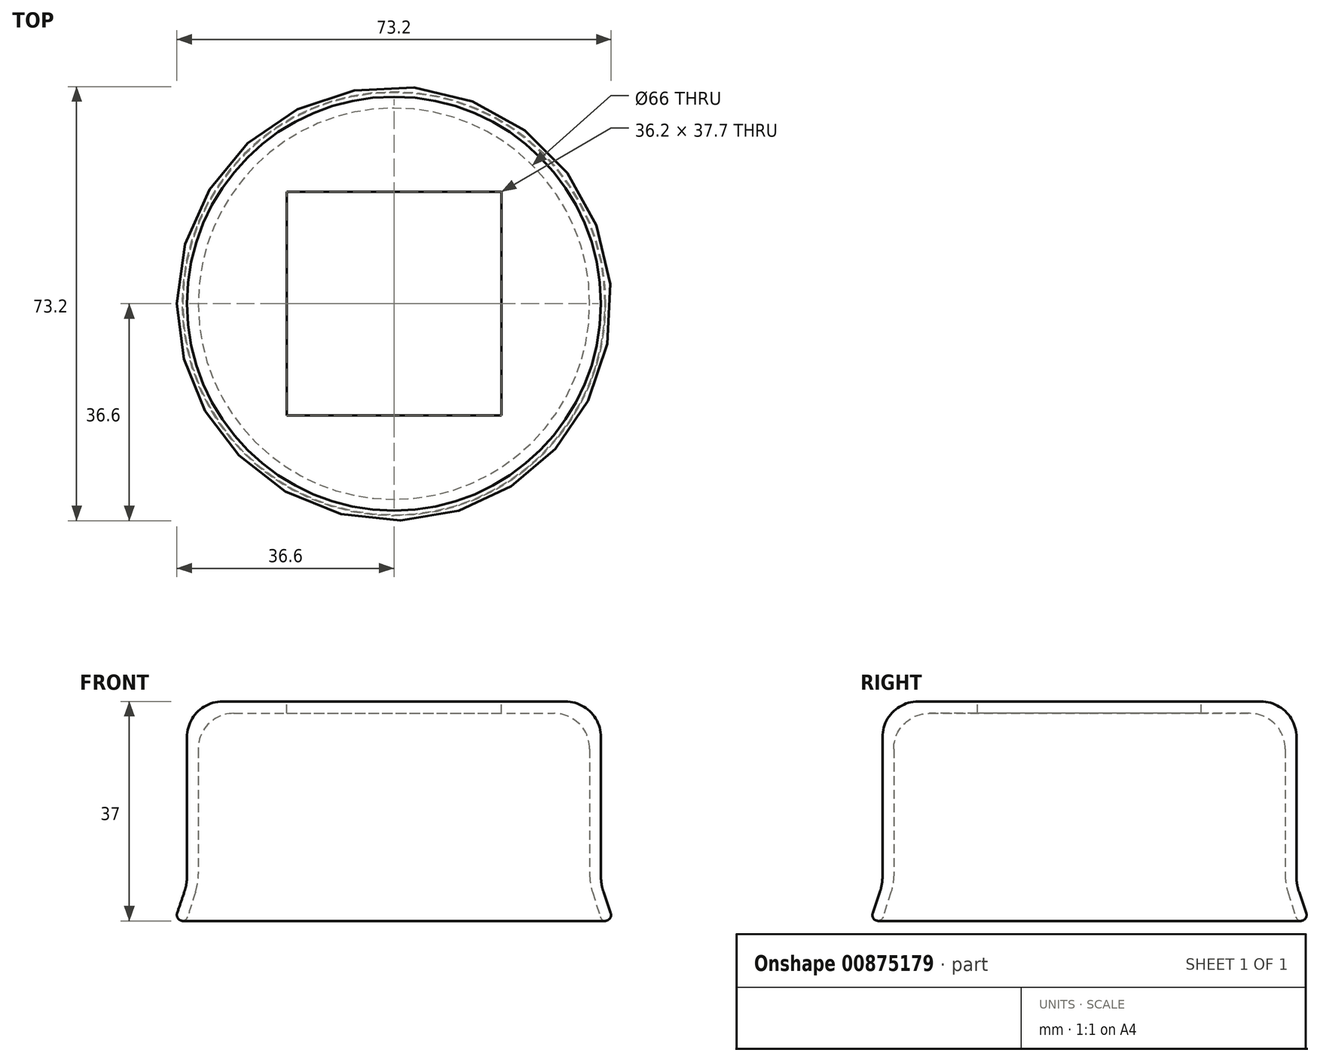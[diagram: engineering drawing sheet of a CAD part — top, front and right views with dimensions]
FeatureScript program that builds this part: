
annotation { "Feature Type Name" : "Feature", "Feature Type Description" : "" }
export const myFeature = defineFeature(function(context is Context, id is Id, definition is map)
    precondition{}
    {
        {
            var Q0;
            Q0=qCreatedBy(makeId("Front.planeOp"),FACE);
            var sketch = newSketch(context, id + "F0", { "sketchPlane" : qUnion([Q0])});
            skLineSegment(sketch, "E0", {"start": v(0, 35) * mm, "end": v(-27, 35) * mm});
            skLineSegment(sketch, "E1", {"start": v(-34.9, 7.5) * mm, "end": v(-34.9, 31) * mm});
            skLineSegment(sketch, "E2", {"start": v(-28.9, 37) * mm, "end": v(0, 37) * mm});
            skLineSegment(sketch, "E3", {"start": v(0, 37) * mm, "end": v(0, 35) * mm});
            skLineSegment(sketch, "E4", {"start": v(-33, 29) * mm, "end": v(-33, 7.9) * mm});
            skPoint(sketch, "E5.visualSharp", {"position": v(-34.9, 37) * mm});
            skArc(sketch, "E5.filletArc", {"start": v(-28.9, 37) * mm, "mid": v(-33.14, 35.24) * mm, "end": v(-34.9, 31) * mm});
            skPoint(sketch, "E6.visualSharp", {"position": v(-33, 35) * mm});
            skArc(sketch, "E6.filletArc", {"start": v(-27, 35) * mm, "mid": v(-31.24, 33.24) * mm, "end": v(-33, 29) * mm});
            skLineSegment(sketch, "E7", {"start": v(-33.46, 4.89) * mm, "end": v(-34.78, 0.7) * mm});
            skLineSegment(sketch, "E8", {"start": v(-35.6, 0) * mm, "end": v(-35.73, 0) * mm});
            skLineSegment(sketch, "E9", {"start": v(-36.55, 1.32) * mm, "end": v(-35.33, 4.91) * mm});
            skPoint(sketch, "E10.visualSharp", {"position": v(-33, 6.35) * mm});
            skArc(sketch, "E10.filletArc", {"start": v(-33.46, 4.89) * mm, "mid": v(-33.12, 6.37) * mm, "end": v(-33, 7.9) * mm});
            skPoint(sketch, "E11.visualSharp", {"position": v(-34.9, 6.17) * mm});
            skArc(sketch, "E11.filletArc", {"start": v(-35.33, 4.91) * mm, "mid": v(-35, 6.18) * mm, "end": v(-34.9, 7.5) * mm});
            skPoint(sketch, "E12.visualSharp", {"position": v(-37, 0) * mm});
            skArc(sketch, "E12.filletArc", {"start": v(-36.55, 1.32) * mm, "mid": v(-36.42, 0.42) * mm, "end": v(-35.6, 0) * mm});
            skPoint(sketch, "E13.visualSharp", {"position": v(-35, 0) * mm});
            skArc(sketch, "E13.filletArc", {"start": v(-35.73, 0) * mm, "mid": v(-35.14, 0.2) * mm, "end": v(-34.78, 0.7) * mm});
            skSolve(sketch);
        }
        {
            var Q0;
            Q0=qCreatedBy(makeId("Front.planeOp"),FACE);
            var sketch = newSketch(context, id + "F1", { "sketchPlane" : qUnion([Q0])});
            skLineSegment(sketch, "E14", {"start": v(0, 0) * mm, "end": v(0, 36.2) * mm, "construction": true});
            skSolve(sketch);
        }
        {
            var Q0;
            Q0=qSketchRegion(id+"F0",true);
            var Q1;
            Q1=sQuery(id+"F1.wireOp",EDGE,"E14");
            revolve(context, id + "F2", {"surfaceOperationType" : NewSurfaceOperationType.NEW, "entities" : qUnion([Q0]), "axis" : qUnion([Q1]), "revolveType" : RevolveType.FULL});
        }
        {
            var Q0;
            Q0=makeQuery(id+"F2.opRevolve","SWEPT_FACE",FACE,{"disambiguationData":[OSD([sQuery(id+"F0.wireOp",EDGE,"E2")])]});
            var sketch = newSketch(context, id + "F3", { "sketchPlane" : qUnion([Q0])});
            skLineSegment(sketch, "E15.bottom", {"start": v(18.1, -18.85) * mm, "end": v(-18.1, -18.85) * mm});
            skLineSegment(sketch, "E15.top", {"start": v(18.1, 18.85) * mm, "end": v(-18.1, 18.85) * mm});
            skLineSegment(sketch, "E15.left", {"start": v(18.1, -18.85) * mm, "end": v(18.1, 18.85) * mm});
            skLineSegment(sketch, "E15.right", {"start": v(-18.1, -18.85) * mm, "end": v(-18.1, 18.85) * mm});
            skPoint(sketch, "E15.middle", {"position": v(0, 0) * mm});
            skSolve(sketch);
        }
        {
            var Q0;
            Q0 = qSketchRegion(id + "F3", true);
            extrude(context, id + "F4", {"entities" : qUnion([Q0]), "operationType" : NewBodyOperationType.REMOVE, "oppositeDirection" : true, "depth" : 25 * mm, "offsetDistance" : 25 * mm});
        }
    });
